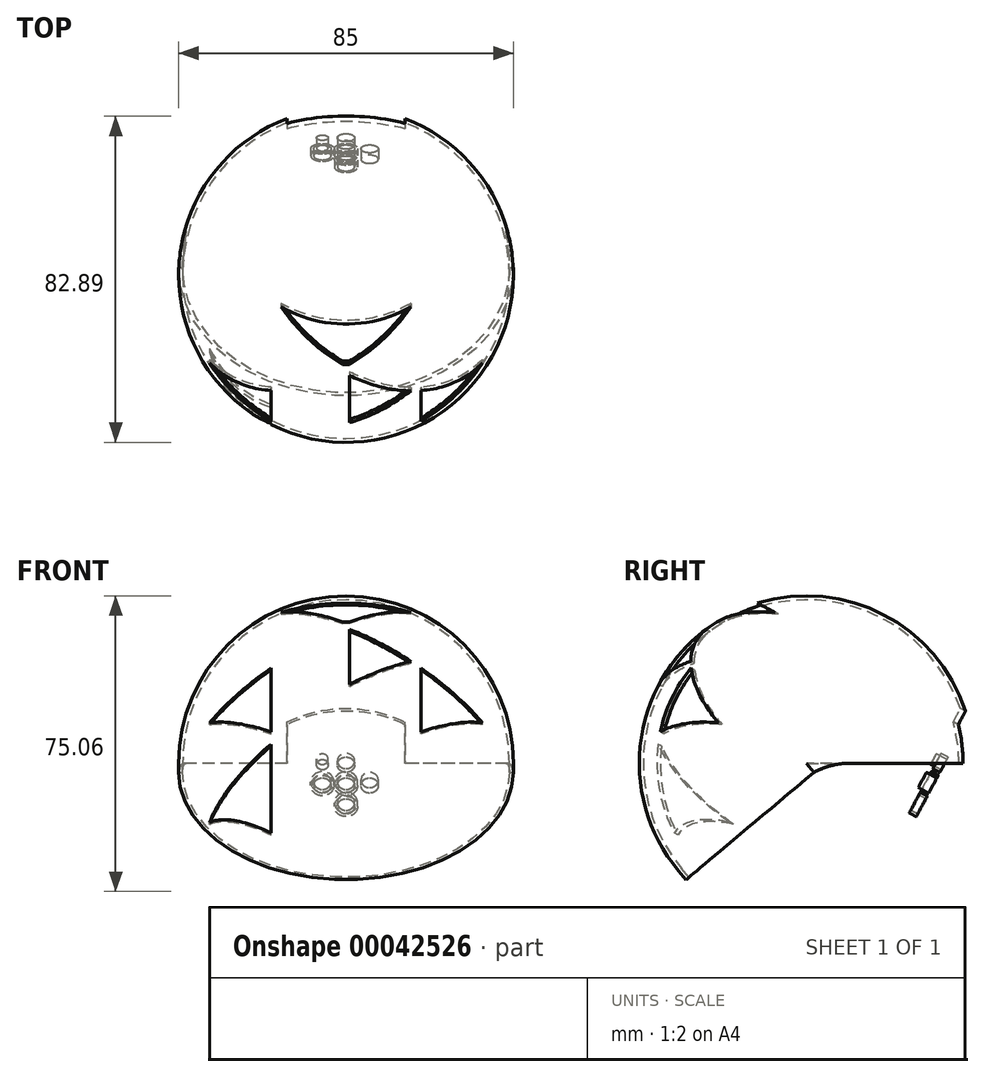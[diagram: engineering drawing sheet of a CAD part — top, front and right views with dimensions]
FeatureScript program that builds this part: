
annotation { "Feature Type Name" : "Feature", "Feature Type Description" : "" }
export const myFeature = defineFeature(function(context is Context, id is Id, definition is map)
    precondition{}
    {
        {
            var Q0;
            Q0=qCreatedBy(makeId("Top.planeOp"),FACE);
            var sketch = newSketch(context, id + "F0", { "sketchPlane" : qUnion([Q0])});
            skArc(sketch, "E0", {"start": v(42.5, 0) * mm, "mid": v(0, 42.5) * mm, "end": v(-42.5, 0) * mm});
            skLineSegment(sketch, "E1", {"start": v(-57, 0) * mm, "end": v(51.83, 0) * mm});
            skSolve(sketch);
        }
        {
            var Q0;
            {var subQ1=sQuery(id+"F0.wireOp",EDGE,"E0");Q0=makeQuery(id+"F0.imprint","IMPRINT",FACE,{"disambiguationData":[TD([[makeQuery(id+"F0.imprint","IMPRINT",EDGE,{"derivedFrom":subQ1}),1.0]])]});}
            var Q1;
            Q1=sQuery(id+"F0.wireOp",EDGE,"E1");
            revolve(context, id + "F1", {"entities" : qUnion([Q0]), "axis" : qUnion([Q1]), "revolveType" : RevolveType.ONE_DIRECTION, "angle" : 220 * degree});
        }
        {
            var Q0;
            Q0=makeQuery(id+"F1.opRevolve","CAP_FACE",FACE,{"disambiguationData":[OSD([sQuery(id+"F0.wireOp",EDGE,"E0"),sQuery(id+"F0.wireOp",EDGE,"E1")])],"isStart":true});
            var Q1;
            Q1=makeQuery(id+"F1.opRevolve","CAP_FACE",FACE,{"disambiguationData":[OSD([sQuery(id+"F0.wireOp",EDGE,"E0"),sQuery(id+"F0.wireOp",EDGE,"E1")])],"isStart":false});
            shell(context, id + "F2", {"entities" : qUnion([Q0, Q1]), "thickness" : 1 * mm});
        }
        {
            var Q0;
            Q0=makeQuery(id+"F1.opRevolve","CAP_FACE",FACE,{"disambiguationData":[OSD([sQuery(id+"F0.wireOp",EDGE,"E0"),sQuery(id+"F0.wireOp",EDGE,"E1")])],"isStart":false});
            extrude(context, id + "F3", {"entities" : qUnion([Q0]), "operationType" : NewBodyOperationType.ADD, "depth" : 3 * mm});
        }
        {
            var Q0;
            Q0=qCreatedBy(makeId("Top.planeOp"),FACE);
            cPlane(context, id + "F4", {"entities" : qUnion([Q0]), "cplaneType" : CPlaneType.OFFSET, "offset" : 28 * mm, "oppositeDirection" : true, "width" : 150 * mm, "height" : 150 * mm});
        }
        {
            var Q0;
            Q0=qCreatedBy(id+"F4.planeOp",FACE);
            var sketch = newSketch(context, id + "F5", { "sketchPlane" : qUnion([Q0])});
            skLineSegment(sketch, "E2", {"start": v(0, 0) * mm, "end": v(0, -48.92) * mm, "construction": true});
            skPoint(sketch, "E3", {"position": v(0, -28.7) * mm});
            skPoint(sketch, "E4", {"position": v(0, -35.7) * mm});
            skLineSegment(sketch, "E5", {"start": v(0, -35.7) * mm, "end": v(-10, -35.7) * mm});
            skPoint(sketch, "E6", {"position": v(0, -26.4) * mm});
            skLineSegment(sketch, "E7", {"start": v(0, -26.4) * mm, "end": v(-10, -26.4) * mm});
            skLineSegment(sketch, "E8", {"start": v(-10, -26.4) * mm, "end": v(-10, -35.7) * mm});
            skLineSegment(sketch, "E9.MirrorCS", {"start": v(0, -35.7) * mm, "end": v(10, -35.7) * mm});
            skLineSegment(sketch, "E10.MirrorCS", {"start": v(10, -26.4) * mm, "end": v(10, -35.7) * mm});
            skLineSegment(sketch, "E11.MirrorCS", {"start": v(0, -26.4) * mm, "end": v(10, -26.4) * mm});
            skSolve(sketch);
        }
        {
            var Q0;
            Q0=makeQuery(id+"F1.opRevolve","CAP_FACE",FACE,{"disambiguationData":[OSD([sQuery(id+"F0.wireOp",EDGE,"E0"),sQuery(id+"F0.wireOp",EDGE,"E1")])],"isStart":true});
            cPlane(context, id + "F6", {"entities" : qUnion([Q0]), "cplaneType" : CPlaneType.OFFSET, "offset" : 0 * mm, "width" : 150 * mm, "height" : 150 * mm});
        }
        {
            var Q0;
            Q0=qCreatedBy(id+"F6.planeOp",FACE);
            var sketch = newSketch(context, id + "F7", { "sketchPlane" : qUnion([Q0])});
            skLineSegment(sketch, "E12", {"start": v(0, 0) * mm, "end": v(40, 0) * mm});
            skLineSegment(sketch, "E13.MirrorCS", {"start": v(0, 0) * mm, "end": v(-40, 0) * mm});
            skSolve(sketch);
        }
        {
            var Q0;
            Q0=sQuery(id+"F7.wireOp",EDGE,"E12");
            cPlane(context, id + "F8", {"entities" : qUnion([Q0]), "cplaneType" : CPlaneType.LINE_ANGLE, "offset" : 150 * mm, "angle" : 62 * degree, "width" : 150 * mm, "height" : 150 * mm});
        }
        {
            var Q0;
            Q0=qCreatedBy(id+"F8.planeOp",FACE);
            var sketch = newSketch(context, id + "F9", { "sketchPlane" : qUnion([Q0])});
            skLineSegment(sketch, "E14", {"start": v(0, 0) * mm, "end": v(0, 38) * mm, "construction": true});
            skPoint(sketch, "E15", {"position": v(0, 33) * mm});
            skPoint(sketch, "E16", {"position": v(0, 31) * mm});
            skLineSegment(sketch, "E17", {"start": v(0, 31) * mm, "end": v(-15, 31) * mm});
            skLineSegment(sketch, "E18", {"start": v(-15, 31) * mm, "end": v(-15, 28) * mm});
            skLineSegment(sketch, "E19", {"start": v(-15, 28) * mm, "end": v(0, 28) * mm});
            skLineSegment(sketch, "E20.MirrorCS", {"start": v(15, 28) * mm, "end": v(0, 28) * mm});
            skLineSegment(sketch, "E21.MirrorCS", {"start": v(15, 31) * mm, "end": v(15, 28) * mm});
            skLineSegment(sketch, "E22.MirrorCS", {"start": v(0, 31) * mm, "end": v(15, 31) * mm});
            skSolve(sketch);
        }
        {
            var Q0;
            Q0=makeQuery(id+"F9.imprint","IMPRINT",FACE,{"disambiguationData":[TD([[makeQuery(id+"F9.imprint","IMPRINT",EDGE,{"derivedFrom":sQuery(id+"F9.wireOp",EDGE,"E17")}),1.0]])]});
            var Q1;
            Q1=makeQuery(id+"F2.opShell","OFFSET_FACE",FACE,{"disambiguationData":[OSD([sQuery(id+"F0.wireOp",EDGE,"E0")])]});
            var Q2;
            Q2=makeQuery(id+"F1.opRevolve","SWEPT_BODY",BODY,{"disambiguationData":[OSD([sQuery(id+"F0.wireOp",EDGE,"E0"),sQuery(id+"F0.wireOp",EDGE,"E1")])]});
            extrude(context, id + "F10", {"entities" : qUnion([Q0]), "operationType" : NewBodyOperationType.ADD, "endBound" : BoundingType.UP_TO_SURFACE, "endBoundEntityFace" : qUnion([Q1]), "endBoundEntityBody" : qUnion([Q2]), "depth" : 25 * mm});
        }
        {
            var Q0;
            Q0=makeQuery(id+"F10.opExtrude","SWEPT_FACE",FACE,{"disambiguationData":[OSD([sQuery(id+"F9.wireOp",EDGE,"E19"),sQuery(id+"F9.wireOp",EDGE,"E20.MirrorCS")])]});
            var sketch = newSketch(context, id + "F11", { "sketchPlane" : qUnion([Q0])});
            skPoint(sketch, "E23", {"position": v(0, 0) * mm});
            skLineSegment(sketch, "E24", {"start": v(0, 0) * mm, "end": v(0, 30.63) * mm, "construction": true});
            skCircle(sketch, "E25", {"center": v(0, 4.05) * mm, "radius": 2.95 * mm});
            skCircle(sketch, "E26", {"center": v(0, 4.05) * mm, "radius": 2.2 * mm});
            skCircle(sketch, "E27", {"center": v(0, 10.05) * mm, "radius": 2.95 * mm});
            skCircle(sketch, "E28", {"center": v(0, 10.05) * mm, "radius": 2.2 * mm});
            skCircle(sketch, "E29", {"center": v(-6, 10.05) * mm, "radius": 2.95 * mm});
            skLineSegment(sketch, "E30", {"start": v(0, 10.05) * mm, "end": v(-6, 10.05) * mm, "construction": true});
            skCircle(sketch, "E31", {"center": v(-6, 10.05) * mm, "radius": 2.2 * mm});
            skCircle(sketch, "E32.MirrorC", {"center": v(6, 10.05) * mm, "radius": 2.95 * mm});
            skCircle(sketch, "E33.MirrorC", {"center": v(6, 10.05) * mm, "radius": 2.2 * mm});
            skCircle(sketch, "E34.MirrorC", {"center": v(0, 16.05) * mm, "radius": 2.2 * mm});
            skCircle(sketch, "E35.MirrorC", {"center": v(0, 16.05) * mm, "radius": 2.95 * mm});
            skPoint(sketch, "E36", {"position": v(6, 16.05) * mm});
            skCircle(sketch, "E37", {"center": v(6, 16.05) * mm, "radius": 1.5 * mm});
            skCircle(sketch, "E38.MirrorC", {"center": v(-6, 16.05) * mm, "radius": 1.5 * mm});
            skSolve(sketch);
        }
        {
            var Q0;
            Q0=makeQuery(id+"F11.imprint","IMPRINT",FACE,{"disambiguationData":[TD([[makeQuery(id+"F11.imprint","IMPRINT",EDGE,{"derivedFrom":sQuery(id+"F11.wireOp",EDGE,"E28")}),1.0]])]});
            var Q1;
            Q1=makeQuery(id+"F11.imprint","IMPRINT",FACE,{"disambiguationData":[TD([[makeQuery(id+"F11.imprint","IMPRINT",EDGE,{"derivedFrom":sQuery(id+"F11.wireOp",EDGE,"E34.MirrorC")}),-1.0]])]});
            var Q2;
            Q2=makeQuery(id+"F11.imprint","IMPRINT",FACE,{"disambiguationData":[TD([[makeQuery(id+"F11.imprint","IMPRINT",EDGE,{"derivedFrom":sQuery(id+"F11.wireOp",EDGE,"E33.MirrorC")}),-1.0]])]});
            var Q3;
            Q3=makeQuery(id+"F11.imprint","IMPRINT",FACE,{"disambiguationData":[TD([[makeQuery(id+"F11.imprint","IMPRINT",EDGE,{"derivedFrom":sQuery(id+"F11.wireOp",EDGE,"E31")}),1.0]])]});
            var Q4;
            Q4=makeQuery(id+"F11.imprint","IMPRINT",FACE,{"disambiguationData":[TD([[makeQuery(id+"F11.imprint","IMPRINT",EDGE,{"derivedFrom":sQuery(id+"F11.wireOp",EDGE,"E26")}),1.0]])]});
            extrude(context, id + "F12", {"entities" : qUnion([Q0, Q1, Q2, Q3, Q4]), "operationType" : NewBodyOperationType.REMOVE, "endBound" : BoundingType.UP_TO_NEXT, "oppositeDirection" : true, "depth" : 25 * mm});
        }
        {
            var Q0;
            Q0=makeQuery(id+"F11.imprint","IMPRINT",FACE,{"disambiguationData":[TD([[makeQuery(id+"F11.imprint","IMPRINT",EDGE,{"derivedFrom":sQuery(id+"F11.wireOp",EDGE,"E29")}),1.0]])]});
            var Q1;
            Q1=makeQuery(id+"F11.imprint","IMPRINT",FACE,{"disambiguationData":[TD([[makeQuery(id+"F11.imprint","IMPRINT",EDGE,{"derivedFrom":sQuery(id+"F11.wireOp",EDGE,"E27")}),1.0]])]});
            var Q2;
            Q2=makeQuery(id+"F11.imprint","IMPRINT",FACE,{"disambiguationData":[TD([[makeQuery(id+"F11.imprint","IMPRINT",EDGE,{"derivedFrom":sQuery(id+"F11.wireOp",EDGE,"E32.MirrorC")}),-1.0]])]});
            var Q3;
            Q3=makeQuery(id+"F11.imprint","IMPRINT",FACE,{"disambiguationData":[TD([[makeQuery(id+"F11.imprint","IMPRINT",EDGE,{"derivedFrom":sQuery(id+"F11.wireOp",EDGE,"E34.MirrorC")}),1.0]])]});
            var Q4;
            Q4=makeQuery(id+"F11.imprint","IMPRINT",FACE,{"disambiguationData":[TD([[makeQuery(id+"F11.imprint","IMPRINT",EDGE,{"derivedFrom":sQuery(id+"F11.wireOp",EDGE,"E25")}),1.0]])]});
            extrude(context, id + "F13", {"entities" : qUnion([Q0, Q1, Q2, Q3, Q4]), "operationType" : NewBodyOperationType.REMOVE, "oppositeDirection" : true, "depth" : 1 * mm});
        }
        {
            var Q0;
            Q0=makeQuery(id+"F11.imprint","IMPRINT",FACE,{"disambiguationData":[TD([[makeQuery(id+"F11.imprint","IMPRINT",EDGE,{"derivedFrom":sQuery(id+"F11.wireOp",EDGE,"E25")}),-1.0]])]});
            cPlane(context, id + "F14", {"entities" : qUnion([Q0]), "cplaneType" : CPlaneType.OFFSET, "offset" : 80 * mm, "width" : 150 * mm, "height" : 150 * mm});
        }
        {
            var Q0;
            Q0=qCreatedBy(id+"F14.planeOp",FACE);
            var sketch = newSketch(context, id + "F15", { "sketchPlane" : qUnion([Q0])});
            skPoint(sketch, "E39", {"position": v(1.77, 0) * mm});
            skLineSegment(sketch, "E40", {"start": v(1.77, 0) * mm, "end": v(1.77, 65.04) * mm, "construction": true});
            skCircle(sketch, "E41", {"center": v(1.77, 9.5) * mm, "radius": 7.5 * mm});
            skCircle(sketch, "E42", {"center": v(1.77, 9.5) * mm, "radius": 8 * mm});
            skSolve(sketch);
        }
        {
            var Q0;
            {var subQ0=sQuery(id+"F0.wireOp",EDGE,"E1");var subQ1=makeQuery(id+"F2.opShell","OFFSET_EDGE",EDGE,{"disambiguationData":[OSD([subQ0])]});Q0=makeQuery(id+"F3.boolean.opBoolean","MERGE",EDGE,{"derivedFrom":[subQ1,makeQuery(id+"F3.opExtrude","CAP_EDGE",EDGE,{"disambiguationData":[OSD([subQ0]),TDD([subQ1])],"isStart":true})]});}
            var Q1;
            {var subQ0=sQuery(id+"F0.wireOp",EDGE,"E1");var subQ1=makeQuery(id+"F1.opRevolve","CAP_EDGE",EDGE,{"disambiguationData":[OSD([subQ0])],"isStart":true});Q1=makeQuery(id+"F3.boolean.opBoolean","MERGE",EDGE,{"derivedFrom":[subQ1,makeQuery(id+"F3.opExtrude","CAP_EDGE",EDGE,{"disambiguationData":[OSD([subQ0]),TDD([subQ1])],"isStart":true})]});}
            fillet(context, id + "F16", {"entities" : qUnion([Q0, Q1]), "radius" : 20 * mm, "tangentPropagation" : true, "allowEdgeOverflow" : false});
        }
        {
            var Q0;
            Q0=qCreatedBy(id+"F14.planeOp",FACE);
            cPlane(context, id + "F17", {"entities" : qUnion([Q0]), "cplaneType" : CPlaneType.OFFSET, "offset" : 20 * mm, "oppositeDirection" : true, "width" : 150 * mm, "height" : 150 * mm});
        }
        {
            var Q0;
            Q0=makeQuery(id+"F11.imprint","IMPRINT",FACE,{"disambiguationData":[TD([[makeQuery(id+"F11.imprint","IMPRINT",EDGE,{"derivedFrom":sQuery(id+"F11.wireOp",EDGE,"E38.MirrorC")}),-1.0]])]});
            var Q1;
            Q1=makeQuery(id+"F11.imprint","IMPRINT",FACE,{"disambiguationData":[TD([[makeQuery(id+"F11.imprint","IMPRINT",EDGE,{"derivedFrom":sQuery(id+"F11.wireOp",EDGE,"E37")}),1.0]])]});
            extrude(context, id + "F18", {"entities" : qUnion([Q0, Q1]), "operationType" : NewBodyOperationType.REMOVE, "oppositeDirection" : true, "depth" : 25 * mm});
        }
        {
            var Q0;
            Q0=qCreatedBy(id+"F14.planeOp",FACE);
            var sketch = newSketch(context, id + "F19", { "sketchPlane" : qUnion([Q0])});
            skCircle(sketch, "E43", {"center": v(0, -1.44) * mm, "radius": 1.5 * mm});
            skCircle(sketch, "E44.cCircle", {"center": v(0, -1.44) * mm, "radius": 1.5 * mm, "construction": true});
            skLineSegment(sketch, "E44.0", {"start": v(0.87, -2.94) * mm, "end": v(-0.87, -2.94) * mm});
            skLineSegment(sketch, "E44.1", {"start": v(-0.87, -2.94) * mm, "end": v(-1.73, -1.44) * mm});
            skLineSegment(sketch, "E44.2", {"start": v(-1.73, -1.44) * mm, "end": v(-0.87, 0.06) * mm});
            skLineSegment(sketch, "E44.3", {"start": v(-0.87, 0.06) * mm, "end": v(0.87, 0.06) * mm});
            skLineSegment(sketch, "E44.4", {"start": v(0.87, 0.06) * mm, "end": v(1.73, -1.44) * mm});
            skLineSegment(sketch, "E44.5", {"start": v(1.73, -1.44) * mm, "end": v(0.87, -2.94) * mm});
            skPoint(sketch, "E44.0.midPoint", {"position": v(0, -2.94) * mm});
            skLineSegment(sketch, "E45", {"start": v(-0.87, -2.94) * mm, "end": v(-0.87, -20.94) * mm});
            skLineSegment(sketch, "E46.MirrorCS", {"start": v(0.87, -20.94) * mm, "end": v(-0.87, -20.94) * mm});
            skCircle(sketch, "E47.MirrorC", {"center": v(0, -22.44) * mm, "radius": 1.5 * mm});
            skLineSegment(sketch, "E48.MirrorCS", {"start": v(1.73, -22.44) * mm, "end": v(0.87, -20.94) * mm});
            skLineSegment(sketch, "E49.MirrorCS", {"start": v(-0.87, -23.94) * mm, "end": v(0.87, -23.94) * mm});
            skCircle(sketch, "E50.MirrorC", {"center": v(0, -22.44) * mm, "radius": 1.5 * mm, "construction": true});
            skPoint(sketch, "E51.MirrorP", {"position": v(0, -20.94) * mm});
            skLineSegment(sketch, "E52.MirrorCS", {"start": v(-0.87, -20.94) * mm, "end": v(-0.87, -2.94) * mm});
            skLineSegment(sketch, "E53.MirrorCS", {"start": v(0.87, -23.94) * mm, "end": v(1.73, -22.44) * mm});
            skLineSegment(sketch, "E54.MirrorCS", {"start": v(-1.73, -22.44) * mm, "end": v(-0.87, -23.94) * mm});
            skLineSegment(sketch, "E55.MirrorCS", {"start": v(-0.87, -20.94) * mm, "end": v(-1.73, -22.44) * mm});
            skLineSegment(sketch, "E56", {"start": v(0.87, -20.94) * mm, "end": v(0.87, -2.94) * mm});
            skLineSegment(sketch, "E57", {"start": v(-0.87, -2.94) * mm, "end": v(-16.45, -11.94) * mm});
            skLineSegment(sketch, "E58", {"start": v(-1.73, -1.44) * mm, "end": v(-17.32, -10.44) * mm});
            skLineSegment(sketch, "E59", {"start": v(-16.45, -11.94) * mm, "end": v(-0.87, -20.94) * mm});
            skLineSegment(sketch, "E60", {"start": v(-1.73, -22.44) * mm, "end": v(-17.32, -13.44) * mm});
            skLineSegment(sketch, "E61", {"start": v(-16.45, -11.94) * mm, "end": v(-20.01, -11.94) * mm, "construction": true});
            skPoint(sketch, "E62", {"position": v(-18.98, -11.94) * mm});
            skCircle(sketch, "E63.MirrorC", {"center": v(-18.19, -11.94) * mm, "radius": 1.5 * mm});
            skLineSegment(sketch, "E64.MirrorCS", {"start": v(-17.32, -10.44) * mm, "end": v(-16.45, -11.94) * mm});
            skLineSegment(sketch, "E65.MirrorCS", {"start": v(-19.92, -11.94) * mm, "end": v(-19.05, -10.44) * mm});
            skLineSegment(sketch, "E66.MirrorCS", {"start": v(-0.87, -20.94) * mm, "end": v(-16.45, -11.94) * mm});
            skLineSegment(sketch, "E67.MirrorCS", {"start": v(-16.45, -11.94) * mm, "end": v(-0.87, -2.94) * mm});
            skLineSegment(sketch, "E68.MirrorCS", {"start": v(-19.05, -13.44) * mm, "end": v(-19.92, -11.94) * mm});
            skPoint(sketch, "E69.MirrorP", {"position": v(-16.89, -11.2) * mm});
            skLineSegment(sketch, "E70.MirrorCS", {"start": v(-19.05, -10.44) * mm, "end": v(-17.32, -10.44) * mm});
            skCircle(sketch, "E71.MirrorC", {"center": v(-18.19, -11.94) * mm, "radius": 1.5 * mm, "construction": true});
            skLineSegment(sketch, "E72.MirrorCS", {"start": v(-17.32, -10.44) * mm, "end": v(-1.73, -1.44) * mm});
            skLineSegment(sketch, "E73.MirrorCS", {"start": v(-16.45, -11.94) * mm, "end": v(-17.32, -13.44) * mm});
            skLineSegment(sketch, "E74.MirrorCS", {"start": v(-17.32, -13.44) * mm, "end": v(-19.05, -13.44) * mm});
            skLineSegment(sketch, "E75.MirrorCS", {"start": v(-17.32, -13.44) * mm, "end": v(-1.73, -22.44) * mm});
            skLineSegment(sketch, "E76.MirrorCS", {"start": v(-17.32, -34.44) * mm, "end": v(-16.45, -32.94) * mm});
            skLineSegment(sketch, "E77.MirrorCS", {"start": v(-16.45, -32.94) * mm, "end": v(-17.32, -31.44) * mm});
            skLineSegment(sketch, "E78.MirrorCS", {"start": v(-0.87, -23.94) * mm, "end": v(-1.73, -22.44) * mm});
            skLineSegment(sketch, "E79.MirrorCS", {"start": v(0.87, -23.94) * mm, "end": v(-0.87, -23.94) * mm});
            skLineSegment(sketch, "E80.MirrorCS", {"start": v(-19.05, -31.44) * mm, "end": v(-19.92, -32.94) * mm});
            skLineSegment(sketch, "E81.MirrorCS", {"start": v(-1.73, -22.44) * mm, "end": v(-0.87, -20.94) * mm});
            skLineSegment(sketch, "E82.MirrorCS", {"start": v(0.87, -20.94) * mm, "end": v(1.73, -22.44) * mm});
            skLineSegment(sketch, "E83.MirrorCS", {"start": v(1.73, -22.44) * mm, "end": v(0.87, -23.94) * mm});
            skLineSegment(sketch, "E84.MirrorCS", {"start": v(-0.87, -20.94) * mm, "end": v(0.87, -20.94) * mm});
            skLineSegment(sketch, "E85.MirrorCS", {"start": v(-19.92, -32.94) * mm, "end": v(-19.05, -34.44) * mm});
            skCircle(sketch, "E86.MirrorC", {"center": v(-18.19, -32.94) * mm, "radius": 1.5 * mm});
            skLineSegment(sketch, "E87.MirrorCS", {"start": v(-1.73, -22.44) * mm, "end": v(-17.32, -31.44) * mm});
            skLineSegment(sketch, "E88.MirrorCS", {"start": v(-19.05, -34.44) * mm, "end": v(-17.32, -34.44) * mm});
            skLineSegment(sketch, "E89.MirrorCS", {"start": v(-0.87, -23.94) * mm, "end": v(-16.45, -32.94) * mm});
            skLineSegment(sketch, "E90.MirrorCS", {"start": v(-17.32, -31.44) * mm, "end": v(-19.05, -31.44) * mm});
            skLineSegment(sketch, "E91.MirrorCS", {"start": v(-16.45, -32.94) * mm, "end": v(-20.01, -32.94) * mm, "construction": true});
            skLineSegment(sketch, "E92.MirrorCS", {"start": v(-17.32, -31.44) * mm, "end": v(-1.73, -22.44) * mm});
            skPoint(sketch, "E93.MirrorP", {"position": v(-18.98, -32.94) * mm});
            skPoint(sketch, "E94.MirrorP", {"position": v(0, -23.94) * mm});
            skPoint(sketch, "E95.MirrorP", {"position": v(-16.89, -33.7) * mm});
            skCircle(sketch, "E96.MirrorC", {"center": v(-18.19, -32.94) * mm, "radius": 1.5 * mm, "construction": true});
            skLineSegment(sketch, "E97.MirrorCS", {"start": v(-16.45, -32.94) * mm, "end": v(-0.87, -23.94) * mm});
            skLineSegment(sketch, "E98.MirrorCS", {"start": v(-0.87, 0.06) * mm, "end": v(-1.73, -1.44) * mm});
            skLineSegment(sketch, "E99.MirrorCS", {"start": v(-1.73, -1.44) * mm, "end": v(-0.87, -2.94) * mm});
            skLineSegment(sketch, "E100.MirrorCS", {"start": v(0.87, 0.06) * mm, "end": v(-0.87, 0.06) * mm});
            skLineSegment(sketch, "E101.MirrorCS", {"start": v(0.87, -2.94) * mm, "end": v(0.87, -20.94) * mm});
            skLineSegment(sketch, "E102.MirrorCS", {"start": v(-17.32, 10.56) * mm, "end": v(-16.45, 9.06) * mm});
            skLineSegment(sketch, "E103.MirrorCS", {"start": v(-0.87, -2.94) * mm, "end": v(0.87, -2.94) * mm});
            skLineSegment(sketch, "E104.MirrorCS", {"start": v(1.73, -1.44) * mm, "end": v(0.87, 0.06) * mm});
            skLineSegment(sketch, "E105.MirrorCS", {"start": v(0.87, -2.94) * mm, "end": v(1.73, -1.44) * mm});
            skLineSegment(sketch, "E106.MirrorCS", {"start": v(-19.92, 9.06) * mm, "end": v(-19.05, 10.56) * mm});
            skLineSegment(sketch, "E107.MirrorCS", {"start": v(-16.45, 9.06) * mm, "end": v(-17.32, 7.56) * mm});
            skLineSegment(sketch, "E108.MirrorCS", {"start": v(-0.87, 18.06) * mm, "end": v(-1.73, 19.56) * mm});
            skLineSegment(sketch, "E109.MirrorCS", {"start": v(-16.45, 9.06) * mm, "end": v(-20.01, 9.06) * mm, "construction": true});
            skCircle(sketch, "E110.MirrorC", {"center": v(-18.19, 9.06) * mm, "radius": 1.5 * mm});
            skLineSegment(sketch, "E111.MirrorCS", {"start": v(0.87, 18.06) * mm, "end": v(-0.87, 18.06) * mm});
            skCircle(sketch, "E112.MirrorC", {"center": v(0, 19.56) * mm, "radius": 1.5 * mm});
            skLineSegment(sketch, "E113.MirrorCS", {"start": v(-0.87, 21.06) * mm, "end": v(0.87, 21.06) * mm});
            skLineSegment(sketch, "E114.MirrorCS", {"start": v(1.73, 19.56) * mm, "end": v(0.87, 18.06) * mm});
            skLineSegment(sketch, "E115.MirrorCS", {"start": v(-1.73, 19.56) * mm, "end": v(-0.87, 21.06) * mm});
            skLineSegment(sketch, "E116.MirrorCS", {"start": v(-17.32, 7.56) * mm, "end": v(-19.05, 7.56) * mm});
            skCircle(sketch, "E117.MirrorC", {"center": v(0, 19.56) * mm, "radius": 1.5 * mm, "construction": true});
            skCircle(sketch, "E118.MirrorC", {"center": v(-18.19, 9.06) * mm, "radius": 1.5 * mm, "construction": true});
            skLineSegment(sketch, "E119.MirrorCS", {"start": v(0.87, 21.06) * mm, "end": v(1.73, 19.56) * mm});
            skLineSegment(sketch, "E120.MirrorCS", {"start": v(-19.05, 10.56) * mm, "end": v(-17.32, 10.56) * mm});
            skLineSegment(sketch, "E121.MirrorCS", {"start": v(-19.05, 7.56) * mm, "end": v(-19.92, 9.06) * mm});
            skLineSegment(sketch, "E122.MirrorCS", {"start": v(-16.45, 9.06) * mm, "end": v(-0.87, 18.06) * mm});
            skLineSegment(sketch, "E123.MirrorCS", {"start": v(-0.87, 18.06) * mm, "end": v(-16.45, 9.06) * mm});
            skLineSegment(sketch, "E124.MirrorCS", {"start": v(-1.73, -1.44) * mm, "end": v(-17.32, 7.56) * mm});
            skLineSegment(sketch, "E125.MirrorCS", {"start": v(-0.87, 18.06) * mm, "end": v(-0.87, 0.06) * mm});
            skLineSegment(sketch, "E126.MirrorCS", {"start": v(-1.73, 19.56) * mm, "end": v(-17.32, 10.56) * mm});
            skLineSegment(sketch, "E127.MirrorCS", {"start": v(-16.45, 9.06) * mm, "end": v(-0.87, 0.06) * mm});
            skLineSegment(sketch, "E128.MirrorCS", {"start": v(-0.87, 0.06) * mm, "end": v(-0.87, 18.06) * mm});
            skPoint(sketch, "E129.MirrorP", {"position": v(-18.98, 9.06) * mm});
            skLineSegment(sketch, "E130.MirrorCS", {"start": v(0.87, 0.06) * mm, "end": v(0.87, 18.06) * mm});
            skLineSegment(sketch, "E131.MirrorCS", {"start": v(-17.32, 7.56) * mm, "end": v(-1.73, -1.44) * mm});
            skPoint(sketch, "E132.MirrorP", {"position": v(0, 18.06) * mm});
            skPoint(sketch, "E133.MirrorP", {"position": v(0, 0.06) * mm});
            skLineSegment(sketch, "E134.MirrorCS", {"start": v(-0.87, 0.06) * mm, "end": v(-16.45, 9.06) * mm});
            skPoint(sketch, "E135.MirrorP", {"position": v(-16.89, 9.8) * mm});
            skLineSegment(sketch, "E136.MirrorCS", {"start": v(-17.32, 10.56) * mm, "end": v(-1.73, 19.56) * mm});
            skLineSegment(sketch, "E137.MirrorCS", {"start": v(-17.32, 28.56) * mm, "end": v(-16.45, 30.06) * mm});
            skLineSegment(sketch, "E138.MirrorCS", {"start": v(-16.45, 30.06) * mm, "end": v(-17.32, 31.56) * mm});
            skCircle(sketch, "E139.MirrorC", {"center": v(-18.19, 30.06) * mm, "radius": 1.5 * mm});
            skLineSegment(sketch, "E140.MirrorCS", {"start": v(-19.05, 31.56) * mm, "end": v(-19.92, 30.06) * mm});
            skLineSegment(sketch, "E141.MirrorCS", {"start": v(-17.32, 31.56) * mm, "end": v(-19.05, 31.56) * mm});
            skCircle(sketch, "E142.MirrorC", {"center": v(-18.19, 30.06) * mm, "radius": 1.5 * mm, "construction": true});
            skLineSegment(sketch, "E143.MirrorCS", {"start": v(-19.05, 28.56) * mm, "end": v(-17.32, 28.56) * mm});
            skLineSegment(sketch, "E144.MirrorCS", {"start": v(-16.45, 30.06) * mm, "end": v(-20.01, 30.06) * mm, "construction": true});
            skLineSegment(sketch, "E145.MirrorCS", {"start": v(-19.92, 30.06) * mm, "end": v(-19.05, 28.56) * mm});
            skPoint(sketch, "E146.MirrorP", {"position": v(-16.89, 29.3) * mm});
            skPoint(sketch, "E147.MirrorP", {"position": v(-18.98, 30.06) * mm});
            skLineSegment(sketch, "E148.MirrorCS", {"start": v(-0.87, 21.06) * mm, "end": v(-16.45, 30.06) * mm});
            skLineSegment(sketch, "E149.MirrorCS", {"start": v(-1.73, 19.56) * mm, "end": v(-17.32, 28.56) * mm});
            skLineSegment(sketch, "E150", {"start": v(-17.32, -31.44) * mm, "end": v(-17.32, -13.44) * mm});
            skLineSegment(sketch, "E151", {"start": v(-19.05, -13.44) * mm, "end": v(-19.05, -31.44) * mm});
            skLineSegment(sketch, "E152", {"start": v(-17.32, -10.44) * mm, "end": v(-17.32, 7.56) * mm});
            skLineSegment(sketch, "E153", {"start": v(-17.32, 10.56) * mm, "end": v(-17.32, 28.56) * mm});
            skLineSegment(sketch, "E154", {"start": v(-19.05, 10.56) * mm, "end": v(-19.05, 28.56) * mm});
            skLineSegment(sketch, "E155", {"start": v(-19.05, 7.56) * mm, "end": v(-19.05, -10.44) * mm});
            skLineSegment(sketch, "E156", {"start": v(-18.19, -32.94) * mm, "end": v(-18.19, -43.9) * mm, "construction": true});
            skPoint(sketch, "E156.endSnap0", {"position": v(-18.19, -34.44) * mm});
            skLineSegment(sketch, "E157.MirrorCS", {"start": v(-35.5, -2.94) * mm, "end": v(-34.64, -1.44) * mm});
            skLineSegment(sketch, "E158.MirrorCS", {"start": v(-34.64, -1.44) * mm, "end": v(-35.5, 0.06) * mm});
            skLineSegment(sketch, "E159.MirrorCS", {"start": v(-37.24, 0.06) * mm, "end": v(-35.5, 0.06) * mm});
            skLineSegment(sketch, "E160.MirrorCS", {"start": v(-34.64, -1.44) * mm, "end": v(-35.5, -2.94) * mm});
            skLineSegment(sketch, "E161.MirrorCS", {"start": v(-35.5, 0.06) * mm, "end": v(-37.24, 0.06) * mm});
            skLineSegment(sketch, "E162.MirrorCS", {"start": v(-37.24, -2.94) * mm, "end": v(-35.5, -2.94) * mm});
            skLineSegment(sketch, "E163.MirrorCS", {"start": v(-35.5, 0.06) * mm, "end": v(-34.64, -1.44) * mm});
            skCircle(sketch, "E164.MirrorC", {"center": v(-36.37, -1.44) * mm, "radius": 1.5 * mm});
            skLineSegment(sketch, "E165.MirrorCS", {"start": v(-37.24, 0.06) * mm, "end": v(-38.1, -1.44) * mm});
            skLineSegment(sketch, "E166.MirrorCS", {"start": v(-35.5, -2.94) * mm, "end": v(-37.24, -2.94) * mm});
            skLineSegment(sketch, "E167.MirrorCS", {"start": v(-37.24, -20.94) * mm, "end": v(-35.5, -20.94) * mm});
            skLineSegment(sketch, "E168.MirrorCS", {"start": v(-35.5, -23.94) * mm, "end": v(-37.24, -23.94) * mm});
            skLineSegment(sketch, "E169.MirrorCS", {"start": v(-34.64, -22.44) * mm, "end": v(-35.5, -20.94) * mm});
            skLineSegment(sketch, "E170.MirrorCS", {"start": v(-38.1, -22.44) * mm, "end": v(-37.24, -20.94) * mm});
            skLineSegment(sketch, "E171.MirrorCS", {"start": v(-38.1, -1.44) * mm, "end": v(-37.24, -2.94) * mm});
            skLineSegment(sketch, "E172.MirrorCS", {"start": v(-35.5, -20.94) * mm, "end": v(-34.64, -22.44) * mm});
            skLineSegment(sketch, "E173.MirrorCS", {"start": v(-37.24, -23.94) * mm, "end": v(-35.5, -23.94) * mm});
            skLineSegment(sketch, "E174.MirrorCS", {"start": v(-37.24, -20.94) * mm, "end": v(-38.1, -22.44) * mm});
            skCircle(sketch, "E175.MirrorC", {"center": v(-36.37, -1.44) * mm, "radius": 1.5 * mm, "construction": true});
            skLineSegment(sketch, "E176.MirrorCS", {"start": v(-38.1, -1.44) * mm, "end": v(-37.24, 0.06) * mm});
            skLineSegment(sketch, "E177.MirrorCS", {"start": v(-35.5, -23.94) * mm, "end": v(-34.64, -22.44) * mm});
            skLineSegment(sketch, "E178.MirrorCS", {"start": v(-37.24, -2.94) * mm, "end": v(-38.1, -1.44) * mm});
            skLineSegment(sketch, "E179.MirrorCS", {"start": v(-34.64, -22.44) * mm, "end": v(-35.5, -23.94) * mm});
            skCircle(sketch, "E180.MirrorC", {"center": v(-36.37, -22.44) * mm, "radius": 1.5 * mm});
            skLineSegment(sketch, "E181.MirrorCS", {"start": v(-35.5, -20.94) * mm, "end": v(-37.24, -20.94) * mm});
            skCircle(sketch, "E182.MirrorC", {"center": v(-36.37, -22.44) * mm, "radius": 1.5 * mm, "construction": true});
            skLineSegment(sketch, "E183.MirrorCS", {"start": v(-38.1, -22.44) * mm, "end": v(-37.24, -23.94) * mm});
            skLineSegment(sketch, "E184.MirrorCS", {"start": v(-35.5, 18.06) * mm, "end": v(-34.64, 19.56) * mm});
            skLineSegment(sketch, "E185.MirrorCS", {"start": v(-35.5, -2.94) * mm, "end": v(-19.92, -11.94) * mm});
            skLineSegment(sketch, "E186.MirrorCS", {"start": v(-37.24, -23.94) * mm, "end": v(-38.1, -22.44) * mm});
            skLineSegment(sketch, "E187.MirrorCS", {"start": v(-35.5, -20.94) * mm, "end": v(-35.5, -2.94) * mm});
            skCircle(sketch, "E188.MirrorC", {"center": v(-36.37, 19.56) * mm, "radius": 1.5 * mm});
            skLineSegment(sketch, "E189.MirrorCS", {"start": v(-19.92, -11.94) * mm, "end": v(-35.5, -2.94) * mm});
            skLineSegment(sketch, "E190.MirrorCS", {"start": v(-34.64, 19.56) * mm, "end": v(-35.5, 21.06) * mm});
            skLineSegment(sketch, "E191.MirrorCS", {"start": v(-19.05, -10.44) * mm, "end": v(-34.64, -1.44) * mm});
            skLineSegment(sketch, "E192.MirrorCS", {"start": v(-37.24, 18.06) * mm, "end": v(-35.5, 18.06) * mm});
            skLineSegment(sketch, "E193.MirrorCS", {"start": v(-35.5, 18.06) * mm, "end": v(-19.92, 9.06) * mm});
            skLineSegment(sketch, "E194.MirrorCS", {"start": v(-37.24, 21.06) * mm, "end": v(-38.1, 19.56) * mm});
            skLineSegment(sketch, "E195.MirrorCS", {"start": v(-34.64, -1.44) * mm, "end": v(-19.05, -10.44) * mm});
            skLineSegment(sketch, "E196.MirrorCS", {"start": v(-35.5, 21.06) * mm, "end": v(-37.24, 21.06) * mm});
            skLineSegment(sketch, "E197.MirrorCS", {"start": v(-38.1, 19.56) * mm, "end": v(-37.24, 18.06) * mm});
            skCircle(sketch, "E198.MirrorC", {"center": v(-36.37, 19.56) * mm, "radius": 1.5 * mm, "construction": true});
            skLineSegment(sketch, "E199.MirrorCS", {"start": v(-35.5, -2.94) * mm, "end": v(-35.5, -20.94) * mm});
            skLineSegment(sketch, "E200.MirrorCS", {"start": v(-34.64, -1.44) * mm, "end": v(-19.05, 7.56) * mm});
            skLineSegment(sketch, "E201.MirrorCS", {"start": v(-35.5, -23.94) * mm, "end": v(-19.92, -32.94) * mm});
            skLineSegment(sketch, "E202.MirrorCS", {"start": v(-19.92, 9.06) * mm, "end": v(-35.5, 0.06) * mm});
            skLineSegment(sketch, "E203.MirrorCS", {"start": v(-19.92, -11.94) * mm, "end": v(-35.5, -20.94) * mm});
            skLineSegment(sketch, "E204.MirrorCS", {"start": v(-35.5, 18.06) * mm, "end": v(-35.5, 0.06) * mm});
            skLineSegment(sketch, "E205.MirrorCS", {"start": v(-34.64, 19.56) * mm, "end": v(-19.05, 10.56) * mm});
            skLineSegment(sketch, "E206.MirrorCS", {"start": v(-19.05, -13.44) * mm, "end": v(-34.64, -22.44) * mm});
            skPoint(sketch, "E207.MirrorP", {"position": v(-36.37, -2.94) * mm});
            skLineSegment(sketch, "E208.MirrorCS", {"start": v(-19.05, -31.44) * mm, "end": v(-34.64, -22.44) * mm});
            skLineSegment(sketch, "E209.MirrorCS", {"start": v(-37.24, -2.94) * mm, "end": v(-37.24, -20.94) * mm});
            skLineSegment(sketch, "E210.MirrorCS", {"start": v(-34.64, -22.44) * mm, "end": v(-19.05, -13.44) * mm});
            skLineSegment(sketch, "E211.MirrorCS", {"start": v(-19.92, 9.06) * mm, "end": v(-35.5, 18.06) * mm});
            skLineSegment(sketch, "E212.MirrorCS", {"start": v(-19.05, 10.56) * mm, "end": v(-34.64, 19.56) * mm});
            skLineSegment(sketch, "E213.MirrorCS", {"start": v(-34.64, -22.44) * mm, "end": v(-19.05, -31.44) * mm});
            skLineSegment(sketch, "E214.MirrorCS", {"start": v(-35.5, 0.06) * mm, "end": v(-19.92, 9.06) * mm});
            skLineSegment(sketch, "E215.MirrorCS", {"start": v(-37.24, -20.94) * mm, "end": v(-37.24, -2.94) * mm});
            skPoint(sketch, "E216.MirrorP", {"position": v(-36.37, 0.06) * mm});
            skLineSegment(sketch, "E217.MirrorCS", {"start": v(-19.92, -32.94) * mm, "end": v(-35.5, -23.94) * mm});
            skLineSegment(sketch, "E218.MirrorCS", {"start": v(-19.05, 7.56) * mm, "end": v(-34.64, -1.44) * mm});
            skPoint(sketch, "E219.MirrorP", {"position": v(-36.37, 18.06) * mm});
            skLineSegment(sketch, "E220.MirrorCS", {"start": v(-35.5, -20.94) * mm, "end": v(-19.92, -11.94) * mm});
            skLineSegment(sketch, "E221.MirrorCS", {"start": v(-37.24, 0.06) * mm, "end": v(-37.24, 18.06) * mm});
            skPoint(sketch, "E222.MirrorP", {"position": v(-36.37, -23.94) * mm});
            skLineSegment(sketch, "E223.MirrorCS", {"start": v(-35.5, 0.06) * mm, "end": v(-35.5, 18.06) * mm});
            skLineSegment(sketch, "E224.MirrorCS", {"start": v(-34.64, 19.56) * mm, "end": v(-19.05, 28.56) * mm});
            skLineSegment(sketch, "E225.MirrorCS", {"start": v(-35.5, 21.06) * mm, "end": v(-19.92, 30.06) * mm});
            skPoint(sketch, "E226.MirrorP", {"position": v(-36.37, -20.94) * mm});
            skLineSegment(sketch, "E227", {"start": v(0, -22.44) * mm, "end": v(0, -33.26) * mm, "construction": true});
            skLineSegment(sketch, "E228.MirrorCS", {"start": v(35.5, -2.94) * mm, "end": v(34.64, -1.44) * mm});
            skLineSegment(sketch, "E229.MirrorCS", {"start": v(34.64, -1.44) * mm, "end": v(35.5, 0.06) * mm});
            skLineSegment(sketch, "E230.MirrorCS", {"start": v(37.24, -2.94) * mm, "end": v(35.5, -2.94) * mm});
            skLineSegment(sketch, "E231.MirrorCS", {"start": v(34.64, -1.44) * mm, "end": v(35.5, -2.94) * mm});
            skCircle(sketch, "E232.MirrorC", {"center": v(36.37, -1.44) * mm, "radius": 1.5 * mm});
            skLineSegment(sketch, "E233.MirrorCS", {"start": v(37.24, 0.06) * mm, "end": v(35.5, 0.06) * mm});
            skLineSegment(sketch, "E234.MirrorCS", {"start": v(37.24, -2.94) * mm, "end": v(38.1, -1.44) * mm});
            skLineSegment(sketch, "E235.MirrorCS", {"start": v(35.5, 0.06) * mm, "end": v(34.64, -1.44) * mm});
            skLineSegment(sketch, "E236.MirrorCS", {"start": v(38.1, -1.44) * mm, "end": v(37.24, -2.94) * mm});
            skLineSegment(sketch, "E237.MirrorCS", {"start": v(37.24, -20.94) * mm, "end": v(35.5, -20.94) * mm});
            skLineSegment(sketch, "E238.MirrorCS", {"start": v(17.32, -10.44) * mm, "end": v(16.45, -11.94) * mm});
            skLineSegment(sketch, "E239.MirrorCS", {"start": v(35.5, -2.94) * mm, "end": v(37.24, -2.94) * mm});
            skLineSegment(sketch, "E240.MirrorCS", {"start": v(35.5, 0.06) * mm, "end": v(37.24, 0.06) * mm});
            skLineSegment(sketch, "E241.MirrorCS", {"start": v(34.64, -22.44) * mm, "end": v(35.5, -20.94) * mm});
            skLineSegment(sketch, "E242.MirrorCS", {"start": v(35.5, -23.94) * mm, "end": v(34.64, -22.44) * mm});
            skCircle(sketch, "E243.MirrorC", {"center": v(36.37, -1.44) * mm, "radius": 1.5 * mm, "construction": true});
            skLineSegment(sketch, "E244.MirrorCS", {"start": v(35.5, -20.94) * mm, "end": v(37.24, -20.94) * mm});
            skLineSegment(sketch, "E245.MirrorCS", {"start": v(35.5, -20.94) * mm, "end": v(34.64, -22.44) * mm});
            skLineSegment(sketch, "E246.MirrorCS", {"start": v(37.24, 0.06) * mm, "end": v(38.1, -1.44) * mm});
            skLineSegment(sketch, "E247.MirrorCS", {"start": v(34.64, -22.44) * mm, "end": v(35.5, -23.94) * mm});
            skCircle(sketch, "E248.MirrorC", {"center": v(36.37, -22.44) * mm, "radius": 1.5 * mm});
            skLineSegment(sketch, "E249.MirrorCS", {"start": v(17.32, 10.56) * mm, "end": v(16.45, 9.06) * mm});
            skLineSegment(sketch, "E250.MirrorCS", {"start": v(35.5, -23.94) * mm, "end": v(37.24, -23.94) * mm});
            skLineSegment(sketch, "E251.MirrorCS", {"start": v(19.05, -10.44) * mm, "end": v(17.32, -10.44) * mm});
            skLineSegment(sketch, "E252.MirrorCS", {"start": v(19.92, -11.94) * mm, "end": v(19.05, -10.44) * mm});
            skLineSegment(sketch, "E253.MirrorCS", {"start": v(17.32, 28.56) * mm, "end": v(16.45, 30.06) * mm});
            skLineSegment(sketch, "E254.MirrorCS", {"start": v(16.45, 30.06) * mm, "end": v(17.32, 31.56) * mm});
            skCircle(sketch, "E255.MirrorC", {"center": v(18.19, 9.06) * mm, "radius": 1.5 * mm});
            skCircle(sketch, "E256.MirrorC", {"center": v(18.19, -11.94) * mm, "radius": 1.5 * mm});
            skLineSegment(sketch, "E257.MirrorCS", {"start": v(38.1, -1.44) * mm, "end": v(37.24, 0.06) * mm});
            skLineSegment(sketch, "E258.MirrorCS", {"start": v(16.45, 9.06) * mm, "end": v(17.32, 7.56) * mm});
            skLineSegment(sketch, "E259.MirrorCS", {"start": v(19.05, 7.56) * mm, "end": v(19.92, 9.06) * mm});
            skLineSegment(sketch, "E260.MirrorCS", {"start": v(16.45, -11.94) * mm, "end": v(17.32, -13.44) * mm});
            skLineSegment(sketch, "E261.MirrorCS", {"start": v(19.92, 9.06) * mm, "end": v(19.05, 10.56) * mm});
            skLineSegment(sketch, "E262.MirrorCS", {"start": v(37.24, -23.94) * mm, "end": v(35.5, -23.94) * mm});
            skLineSegment(sketch, "E263.MirrorCS", {"start": v(17.32, -31.44) * mm, "end": v(19.05, -31.44) * mm});
            skCircle(sketch, "E264.MirrorC", {"center": v(18.19, 30.06) * mm, "radius": 1.5 * mm});
            skLineSegment(sketch, "E265.MirrorCS", {"start": v(16.45, -32.94) * mm, "end": v(17.32, -31.44) * mm});
            skLineSegment(sketch, "E266.MirrorCS", {"start": v(17.32, -13.44) * mm, "end": v(19.05, -13.44) * mm});
            skLineSegment(sketch, "E267.MirrorCS", {"start": v(38.1, -22.44) * mm, "end": v(37.24, -20.94) * mm});
            skCircle(sketch, "E268.MirrorC", {"center": v(18.19, 9.06) * mm, "radius": 1.5 * mm, "construction": true});
            skLineSegment(sketch, "E269.MirrorCS", {"start": v(38.1, -22.44) * mm, "end": v(37.24, -23.94) * mm});
            skLineSegment(sketch, "E270.MirrorCS", {"start": v(19.05, 10.56) * mm, "end": v(17.32, 10.56) * mm});
            skCircle(sketch, "E271.MirrorC", {"center": v(36.37, -22.44) * mm, "radius": 1.5 * mm, "construction": true});
            skCircle(sketch, "E272.MirrorC", {"center": v(18.19, -11.94) * mm, "radius": 1.5 * mm, "construction": true});
            skLineSegment(sketch, "E273.MirrorCS", {"start": v(19.05, -13.44) * mm, "end": v(19.92, -11.94) * mm});
            skLineSegment(sketch, "E274.MirrorCS", {"start": v(35.5, 18.06) * mm, "end": v(34.64, 19.56) * mm});
            skLineSegment(sketch, "E275.MirrorCS", {"start": v(19.05, -31.44) * mm, "end": v(19.92, -32.94) * mm});
            skLineSegment(sketch, "E276.MirrorCS", {"start": v(17.32, 7.56) * mm, "end": v(19.05, 7.56) * mm});
            skLineSegment(sketch, "E277.MirrorCS", {"start": v(17.32, -34.44) * mm, "end": v(16.45, -32.94) * mm});
            skLineSegment(sketch, "E278.MirrorCS", {"start": v(19.92, -11.94) * mm, "end": v(35.5, -2.94) * mm});
            skLineSegment(sketch, "E279.MirrorCS", {"start": v(0.87, -2.94) * mm, "end": v(16.45, -11.94) * mm});
            skLineSegment(sketch, "E280.MirrorCS", {"start": v(16.45, -32.94) * mm, "end": v(20.01, -32.94) * mm, "construction": true});
            skLineSegment(sketch, "E281.MirrorCS", {"start": v(19.05, 31.56) * mm, "end": v(19.92, 30.06) * mm});
            skCircle(sketch, "E282.MirrorC", {"center": v(18.19, 30.06) * mm, "radius": 1.5 * mm, "construction": true});
            skLineSegment(sketch, "E283.MirrorCS", {"start": v(37.24, -23.94) * mm, "end": v(38.1, -22.44) * mm});
            skLineSegment(sketch, "E284.MirrorCS", {"start": v(19.92, 30.06) * mm, "end": v(19.05, 28.56) * mm});
            skLineSegment(sketch, "E285.MirrorCS", {"start": v(19.05, 28.56) * mm, "end": v(17.32, 28.56) * mm});
            skLineSegment(sketch, "E286.MirrorCS", {"start": v(37.24, -20.94) * mm, "end": v(38.1, -22.44) * mm});
            skLineSegment(sketch, "E287.MirrorCS", {"start": v(17.32, -10.44) * mm, "end": v(1.73, -1.44) * mm});
            skLineSegment(sketch, "E288.MirrorCS", {"start": v(35.5, -20.94) * mm, "end": v(35.5, -2.94) * mm});
            skLineSegment(sketch, "E289.MirrorCS", {"start": v(19.05, -10.44) * mm, "end": v(34.64, -1.44) * mm});
            skCircle(sketch, "E290.MirrorC", {"center": v(36.37, 19.56) * mm, "radius": 1.5 * mm});
            skLineSegment(sketch, "E291.MirrorCS", {"start": v(16.45, -11.94) * mm, "end": v(20.01, -11.94) * mm, "construction": true});
            skLineSegment(sketch, "E292.MirrorCS", {"start": v(16.45, 9.06) * mm, "end": v(20.01, 9.06) * mm, "construction": true});
            skLineSegment(sketch, "E293.MirrorCS", {"start": v(35.5, -2.94) * mm, "end": v(19.92, -11.94) * mm});
            skLineSegment(sketch, "E294.MirrorCS", {"start": v(34.64, 19.56) * mm, "end": v(35.5, 21.06) * mm});
            skLineSegment(sketch, "E295.MirrorCS", {"start": v(16.45, -11.94) * mm, "end": v(0.87, -2.94) * mm});
            skLineSegment(sketch, "E296.MirrorCS", {"start": v(37.24, 18.06) * mm, "end": v(35.5, 18.06) * mm});
            skCircle(sketch, "E297.MirrorC", {"center": v(18.19, -32.94) * mm, "radius": 1.5 * mm});
            skLineSegment(sketch, "E298.MirrorCS", {"start": v(38.1, 19.56) * mm, "end": v(37.24, 18.06) * mm});
            skLineSegment(sketch, "E299.MirrorCS", {"start": v(0.87, 18.06) * mm, "end": v(16.45, 9.06) * mm});
            skLineSegment(sketch, "E300.MirrorCS", {"start": v(35.5, -2.94) * mm, "end": v(35.5, -20.94) * mm});
            skLineSegment(sketch, "E301.MirrorCS", {"start": v(35.5, 18.06) * mm, "end": v(19.92, 9.06) * mm});
            skCircle(sketch, "E302.MirrorC", {"center": v(18.19, -32.94) * mm, "radius": 1.5 * mm, "construction": true});
            skLineSegment(sketch, "E303.MirrorCS", {"start": v(19.05, -34.44) * mm, "end": v(17.32, -34.44) * mm});
            skLineSegment(sketch, "E304.MirrorCS", {"start": v(1.73, -1.44) * mm, "end": v(17.32, -10.44) * mm});
            skLineSegment(sketch, "E305.MirrorCS", {"start": v(37.24, 21.06) * mm, "end": v(38.1, 19.56) * mm});
            skCircle(sketch, "E306.MirrorC", {"center": v(36.37, 19.56) * mm, "radius": 1.5 * mm, "construction": true});
            skLineSegment(sketch, "E307.MirrorCS", {"start": v(35.5, 21.06) * mm, "end": v(37.24, 21.06) * mm});
            skLineSegment(sketch, "E308.MirrorCS", {"start": v(19.92, -32.94) * mm, "end": v(19.05, -34.44) * mm});
            skLineSegment(sketch, "E309.MirrorCS", {"start": v(16.45, 30.06) * mm, "end": v(20.01, 30.06) * mm, "construction": true});
            skLineSegment(sketch, "E310.MirrorCS", {"start": v(0.87, -23.94) * mm, "end": v(16.45, -32.94) * mm});
            skLineSegment(sketch, "E311.MirrorCS", {"start": v(17.32, -13.44) * mm, "end": v(1.73, -22.44) * mm});
            skLineSegment(sketch, "E312.MirrorCS", {"start": v(16.45, -11.94) * mm, "end": v(0.87, -20.94) * mm});
            skLineSegment(sketch, "E313.MirrorCS", {"start": v(34.64, -22.44) * mm, "end": v(19.05, -31.44) * mm});
            skLineSegment(sketch, "E314.MirrorCS", {"start": v(35.5, 0.06) * mm, "end": v(19.92, 9.06) * mm});
            skLineSegment(sketch, "E315.MirrorCS", {"start": v(1.73, -1.44) * mm, "end": v(17.32, 7.56) * mm});
            skLineSegment(sketch, "E316.MirrorCS", {"start": v(37.24, -20.94) * mm, "end": v(37.24, -2.94) * mm});
            skLineSegment(sketch, "E317.MirrorCS", {"start": v(19.92, -32.94) * mm, "end": v(35.5, -23.94) * mm});
            skLineSegment(sketch, "E318.MirrorCS", {"start": v(17.32, -31.44) * mm, "end": v(1.73, -22.44) * mm});
            skLineSegment(sketch, "E319.MirrorCS", {"start": v(1.73, 19.56) * mm, "end": v(17.32, 10.56) * mm});
            skLineSegment(sketch, "E320.MirrorCS", {"start": v(19.05, 7.56) * mm, "end": v(34.64, -1.44) * mm});
            skLineSegment(sketch, "E321.MirrorCS", {"start": v(35.5, -20.94) * mm, "end": v(19.92, -11.94) * mm});
            skPoint(sketch, "E322.MirrorP", {"position": v(36.37, -2.94) * mm});
            skLineSegment(sketch, "E323.MirrorCS", {"start": v(34.64, -1.44) * mm, "end": v(19.05, -10.44) * mm});
            skLineSegment(sketch, "E324.MirrorCS", {"start": v(34.64, 19.56) * mm, "end": v(19.05, 10.56) * mm});
            skLineSegment(sketch, "E325.MirrorCS", {"start": v(35.5, 0.06) * mm, "end": v(35.5, 18.06) * mm});
            skLineSegment(sketch, "E326.MirrorCS", {"start": v(16.45, 9.06) * mm, "end": v(0.87, 0.06) * mm});
            skLineSegment(sketch, "E327.MirrorCS", {"start": v(19.05, -13.44) * mm, "end": v(34.64, -22.44) * mm});
            skPoint(sketch, "E328.MirrorP", {"position": v(36.37, 18.06) * mm});
            skPoint(sketch, "E329.MirrorP", {"position": v(18.19, -34.44) * mm});
            skLineSegment(sketch, "E330.MirrorCS", {"start": v(19.05, 7.56) * mm, "end": v(19.05, -10.44) * mm});
            skPoint(sketch, "E331.MirrorP", {"position": v(36.37, -23.94) * mm});
            skLineSegment(sketch, "E332.MirrorCS", {"start": v(18.19, -32.94) * mm, "end": v(18.19, -43.9) * mm, "construction": true});
            skLineSegment(sketch, "E333.MirrorCS", {"start": v(19.92, 9.06) * mm, "end": v(35.5, 0.06) * mm});
            skLineSegment(sketch, "E334.MirrorCS", {"start": v(1.73, -22.44) * mm, "end": v(17.32, -13.44) * mm});
            skPoint(sketch, "E335.MirrorP", {"position": v(36.37, -20.94) * mm});
            skPoint(sketch, "E336.MirrorP", {"position": v(18.98, -11.94) * mm});
            skLineSegment(sketch, "E337.MirrorCS", {"start": v(19.92, -11.94) * mm, "end": v(35.5, -20.94) * mm});
            skLineSegment(sketch, "E338.MirrorCS", {"start": v(0.87, -20.94) * mm, "end": v(16.45, -11.94) * mm});
            skLineSegment(sketch, "E339.MirrorCS", {"start": v(35.5, -23.94) * mm, "end": v(19.92, -32.94) * mm});
            skLineSegment(sketch, "E340.MirrorCS", {"start": v(19.05, 10.56) * mm, "end": v(19.05, 28.56) * mm});
            skLineSegment(sketch, "E341.MirrorCS", {"start": v(16.45, 9.06) * mm, "end": v(0.87, 18.06) * mm});
            skPoint(sketch, "E342.MirrorP", {"position": v(18.98, 30.06) * mm});
            skLineSegment(sketch, "E343.MirrorCS", {"start": v(34.64, -1.44) * mm, "end": v(19.05, 7.56) * mm});
            skLineSegment(sketch, "E344.MirrorCS", {"start": v(19.05, 10.56) * mm, "end": v(34.64, 19.56) * mm});
            skLineSegment(sketch, "E345.MirrorCS", {"start": v(17.32, 10.56) * mm, "end": v(17.32, 28.56) * mm});
            skLineSegment(sketch, "E346.MirrorCS", {"start": v(17.32, 10.56) * mm, "end": v(1.73, 19.56) * mm});
            skPoint(sketch, "E347.MirrorP", {"position": v(16.89, 29.3) * mm});
            skPoint(sketch, "E348.MirrorP", {"position": v(36.37, 0.06) * mm});
            skLineSegment(sketch, "E349.MirrorCS", {"start": v(1.73, -22.44) * mm, "end": v(17.32, -31.44) * mm});
            skLineSegment(sketch, "E350.MirrorCS", {"start": v(16.45, -32.94) * mm, "end": v(0.87, -23.94) * mm});
            skPoint(sketch, "E351.MirrorP", {"position": v(16.89, -11.2) * mm});
            skLineSegment(sketch, "E352.MirrorCS", {"start": v(17.32, -31.44) * mm, "end": v(17.32, -13.44) * mm});
            skLineSegment(sketch, "E353.MirrorCS", {"start": v(34.64, -22.44) * mm, "end": v(19.05, -13.44) * mm});
            skLineSegment(sketch, "E354.MirrorCS", {"start": v(17.32, -10.44) * mm, "end": v(17.32, 7.56) * mm});
            skLineSegment(sketch, "E355.MirrorCS", {"start": v(1.73, 19.56) * mm, "end": v(17.32, 28.56) * mm});
            skLineSegment(sketch, "E356.MirrorCS", {"start": v(37.24, -2.94) * mm, "end": v(37.24, -20.94) * mm});
            skLineSegment(sketch, "E357.MirrorCS", {"start": v(35.5, 21.06) * mm, "end": v(19.92, 30.06) * mm});
            skPoint(sketch, "E358.MirrorP", {"position": v(18.98, -32.94) * mm});
            skLineSegment(sketch, "E359.MirrorCS", {"start": v(0.87, 0.06) * mm, "end": v(16.45, 9.06) * mm});
            skPoint(sketch, "E360.MirrorP", {"position": v(16.89, 9.8) * mm});
            skLineSegment(sketch, "E361.MirrorCS", {"start": v(19.05, -13.44) * mm, "end": v(19.05, -31.44) * mm});
            skPoint(sketch, "E362.MirrorP", {"position": v(18.98, 9.06) * mm});
            skLineSegment(sketch, "E363.MirrorCS", {"start": v(37.24, 0.06) * mm, "end": v(37.24, 18.06) * mm});
            skLineSegment(sketch, "E364.MirrorCS", {"start": v(19.92, 9.06) * mm, "end": v(35.5, 18.06) * mm});
            skLineSegment(sketch, "E365.MirrorCS", {"start": v(35.5, 18.06) * mm, "end": v(35.5, 0.06) * mm});
            skLineSegment(sketch, "E366.MirrorCS", {"start": v(34.64, 19.56) * mm, "end": v(19.05, 28.56) * mm});
            skPoint(sketch, "E367.MirrorP", {"position": v(16.89, -33.7) * mm});
            skLineSegment(sketch, "E368.MirrorCS", {"start": v(19.05, -31.44) * mm, "end": v(34.64, -22.44) * mm});
            skLineSegment(sketch, "E369.MirrorCS", {"start": v(17.32, 7.56) * mm, "end": v(1.73, -1.44) * mm});
            skLineSegment(sketch, "E370.MirrorCS", {"start": v(0.87, 21.06) * mm, "end": v(16.45, 30.06) * mm});
            skLineSegment(sketch, "E371", {"start": v(-16.45, -32.94) * mm, "end": v(16.45, -32.94) * mm});
            skLineSegment(sketch, "E372", {"start": v(-16.45, 30.06) * mm, "end": v(16.45, 30.06) * mm});
            skLineSegment(sketch, "E373", {"start": v(0, 19.56) * mm, "end": v(-76.4, 19.56) * mm, "construction": true});
            skLineSegment(sketch, "E374.MirrorCS", {"start": v(17.32, 31.56) * mm, "end": v(19.05, 31.56) * mm});
            skLineSegment(sketch, "E375.MirrorCS", {"start": v(-19.92, 30.06) * mm, "end": v(-35.5, 21.06) * mm});
            skLineSegment(sketch, "E376.MirrorCS", {"start": v(19.05, 28.56) * mm, "end": v(34.64, 19.56) * mm});
            skLineSegment(sketch, "E377.MirrorCS", {"start": v(19.92, 30.06) * mm, "end": v(35.5, 21.06) * mm});
            skLineSegment(sketch, "E378.MirrorCS", {"start": v(17.32, 28.56) * mm, "end": v(1.73, 19.56) * mm});
            skLineSegment(sketch, "E379.MirrorCS", {"start": v(-17.32, 28.56) * mm, "end": v(-1.73, 19.56) * mm});
            skLineSegment(sketch, "E380.MirrorCS", {"start": v(-16.45, 30.06) * mm, "end": v(-0.87, 21.06) * mm});
            skLineSegment(sketch, "E381.MirrorCS", {"start": v(17.32, 28.56) * mm, "end": v(17.32, 10.56) * mm});
            skLineSegment(sketch, "E382.MirrorCS", {"start": v(-17.32, 28.56) * mm, "end": v(-17.32, 10.56) * mm});
            skLineSegment(sketch, "E383.MirrorCS", {"start": v(-19.05, 28.56) * mm, "end": v(-34.64, 19.56) * mm});
            skLineSegment(sketch, "E384.MirrorCS", {"start": v(-19.05, 28.56) * mm, "end": v(-19.05, 10.56) * mm});
            skLineSegment(sketch, "E385.MirrorCS", {"start": v(19.05, 28.56) * mm, "end": v(19.05, 10.56) * mm});
            skLineSegment(sketch, "E386.MirrorCS", {"start": v(16.45, 30.06) * mm, "end": v(0.87, 21.06) * mm});
            skSolve(sketch);
        }
        {
            var Q0;
            Q0=makeQuery(id+"F19.imprint","IMPRINT",FACE,{"disambiguationData":[TD([[makeQuery(id+"F19.imprint","IMPRINT",EDGE,{"derivedFrom":sQuery(id+"F19.wireOp",EDGE,"E130.MirrorCS")}),-1.0]])]});
            var Q1;
            Q1=makeQuery(id+"F19.imprint","IMPRINT",FACE,{"disambiguationData":[TD([[makeQuery(id+"F19.imprint","IMPRINT",EDGE,{"derivedFrom":sQuery(id+"F19.wireOp",EDGE,"E128.MirrorCS")}),1.0]])]});
            var Q2;
            Q2=makeQuery(id+"F19.imprint","IMPRINT",FACE,{"disambiguationData":[TD([[makeQuery(id+"F19.imprint","IMPRINT",EDGE,{"derivedFrom":sQuery(id+"F19.wireOp",EDGE,"E136.MirrorCS")}),1.0]])]});
            var Q3;
            Q3=makeQuery(id+"F19.imprint","IMPRINT",FACE,{"disambiguationData":[TD([[makeQuery(id+"F19.imprint","IMPRINT",EDGE,{"derivedFrom":sQuery(id+"F19.wireOp",EDGE,"E212.MirrorCS")}),-1.0]])]});
            var Q4;
            Q4=makeQuery(id+"F19.imprint","IMPRINT",FACE,{"disambiguationData":[TD([[makeQuery(id+"F19.imprint","IMPRINT",EDGE,{"derivedFrom":sQuery(id+"F19.wireOp",EDGE,"E155")}),-1.0]])]});
            var Q5;
            Q5=makeQuery(id+"F19.imprint","IMPRINT",FACE,{"disambiguationData":[TD([[makeQuery(id+"F19.imprint","IMPRINT",EDGE,{"derivedFrom":sQuery(id+"F19.wireOp",EDGE,"E211.MirrorCS")}),1.0]])]});
            var Q6;
            Q6=makeQuery(id+"F19.imprint","IMPRINT",FACE,{"disambiguationData":[TD([[makeQuery(id+"F19.imprint","IMPRINT",EDGE,{"derivedFrom":sQuery(id+"F19.wireOp",EDGE,"E185.MirrorCS")}),-1.0]])]});
            var Q7;
            Q7=makeQuery(id+"F19.imprint","IMPRINT",FACE,{"disambiguationData":[TD([[makeQuery(id+"F19.imprint","IMPRINT",EDGE,{"derivedFrom":sQuery(id+"F19.wireOp",EDGE,"E151")}),-1.0]])]});
            var Q8;
            Q8=makeQuery(id+"F19.imprint","IMPRINT",FACE,{"disambiguationData":[TD([[makeQuery(id+"F19.imprint","IMPRINT",EDGE,{"derivedFrom":sQuery(id+"F19.wireOp",EDGE,"E75.MirrorCS")}),-1.0]])]});
            var Q9;
            Q9=makeQuery(id+"F19.imprint","IMPRINT",FACE,{"disambiguationData":[TD([[makeQuery(id+"F19.imprint","IMPRINT",EDGE,{"derivedFrom":sQuery(id+"F19.wireOp",EDGE,"E131.MirrorCS")}),-1.0]])]});
            var Q10;
            Q10=makeQuery(id+"F19.imprint","IMPRINT",FACE,{"disambiguationData":[TD([[makeQuery(id+"F19.imprint","IMPRINT",EDGE,{"derivedFrom":sQuery(id+"F19.wireOp",EDGE,"E66.MirrorCS")}),-1.0]])]});
            var Q11;
            Q11=makeQuery(id+"F19.imprint","IMPRINT",FACE,{"disambiguationData":[TD([[makeQuery(id+"F19.imprint","IMPRINT",EDGE,{"derivedFrom":sQuery(id+"F19.wireOp",EDGE,"E101.MirrorCS")}),1.0]])]});
            var Q12;
            Q12=makeQuery(id+"F19.imprint","IMPRINT",FACE,{"disambiguationData":[TD([[makeQuery(id+"F19.imprint","IMPRINT",EDGE,{"derivedFrom":sQuery(id+"F19.wireOp",EDGE,"E304.MirrorCS")}),1.0]])]});
            var Q13;
            Q13=makeQuery(id+"F19.imprint","IMPRINT",FACE,{"disambiguationData":[TD([[makeQuery(id+"F19.imprint","IMPRINT",EDGE,{"derivedFrom":sQuery(id+"F19.wireOp",EDGE,"E334.MirrorCS")}),-1.0]])]});
            var Q14;
            Q14=makeQuery(id+"F19.imprint","IMPRINT",FACE,{"disambiguationData":[TD([[makeQuery(id+"F19.imprint","IMPRINT",EDGE,{"derivedFrom":sQuery(id+"F19.wireOp",EDGE,"E330.MirrorCS")}),1.0]])]});
            var Q15;
            Q15=makeQuery(id+"F19.imprint","IMPRINT",FACE,{"disambiguationData":[TD([[makeQuery(id+"F19.imprint","IMPRINT",EDGE,{"derivedFrom":sQuery(id+"F19.wireOp",EDGE,"E333.MirrorCS")}),1.0]])]});
            var Q16;
            Q16=makeQuery(id+"F19.imprint","IMPRINT",FACE,{"disambiguationData":[TD([[makeQuery(id+"F19.imprint","IMPRINT",EDGE,{"derivedFrom":sQuery(id+"F19.wireOp",EDGE,"E344.MirrorCS")}),1.0]])]});
            var Q17;
            Q17=makeQuery(id+"F19.imprint","IMPRINT",FACE,{"disambiguationData":[TD([[makeQuery(id+"F19.imprint","IMPRINT",EDGE,{"derivedFrom":sQuery(id+"F19.wireOp",EDGE,"E346.MirrorCS")}),-1.0]])]});
            var Q18;
            Q18=makeQuery(id+"F19.imprint","IMPRINT",FACE,{"disambiguationData":[TD([[makeQuery(id+"F19.imprint","IMPRINT",EDGE,{"derivedFrom":sQuery(id+"F19.wireOp",EDGE,"E353.MirrorCS")}),1.0]])]});
            var Q19;
            {var subQ1=sQuery(id+"F19.wireOp",EDGE,"E97.MirrorCS");Q19=makeQuery(id+"F19.imprint","IMPRINT",FACE,{"disambiguationData":[TD([[makeQuery(id+"F19.imprint","IMPRINT",EDGE,{"derivedFrom":subQ1}),-1.0]])]});}
            var Q20;
            Q20=makeQuery(id+"F19.imprint","IMPRINT",FACE,{"disambiguationData":[TD([[makeQuery(id+"F19.imprint","IMPRINT",EDGE,{"derivedFrom":sQuery(id+"F19.wireOp",EDGE,"E75.MirrorCS")}),-1.0]])]});
            var Q21;
            Q21=makeQuery(id+"F19.imprint","IMPRINT",FACE,{"disambiguationData":[TD([[makeQuery(id+"F19.imprint","IMPRINT",EDGE,{"derivedFrom":sQuery(id+"F19.wireOp",EDGE,"E337.MirrorCS")}),1.0]])]});
            var Q22;
            Q22=makeQuery(id+"F19.imprint","IMPRINT",FACE,{"disambiguationData":[TD([[makeQuery(id+"F19.imprint","IMPRINT",EDGE,{"derivedFrom":sQuery(id+"F19.wireOp",EDGE,"E372")}),-1.0]])]});
            extrude(context, id + "F20", {"entities" : qUnion([Q0, Q1, Q2, Q3, Q4, Q5, Q6, Q7, Q8, Q9, Q10, Q11, Q12, Q13, Q14, Q15, Q16, Q17, Q18, Q19, Q20, Q21, Q22]), "operationType" : NewBodyOperationType.REMOVE, "endBound" : BoundingType.UP_TO_NEXT, "oppositeDirection" : true, "depth" : 10 * mm, "hasOffset" : true, "offsetDistance" : 1 * mm, "offsetOppositeDirection" : true});
        }
    });
